# Revit family: Bordo-Basin
name_source: partatom
category: Plumbing Fixtures
units: mm (PartAtom-declared; Revit-internal decimal feet)

## family parameters
Always vertical = Yes
Cut with Voids When Loaded = No
Enable Cutting in Views = No
Maintain Annotation Orientation = No
Part Type = Normal
Room Calculation Point = No
Round Connector Dimension = Use Diameter
Shared = No
Work Plane-Based = No

## types (1)
- Lecico WHB Bordo Counter
    Color = White
    Default Elevation = 0 mm  [stored 0 ft]
    Height of WHB = 600 mm
    Manufacturer = LECICO Quality Bathroom Ceramics
    Mass = 15.00 kg
    Material = Vitreous China
    Parts Code = CTOP024
    Silver = Chrome
    Tolani Civil Projects cc URL = www.tcpbim.co.za
    URL = http://www.lecicosa.co.za

note: [stored X ft] marks values corroborated as IEEE doubles in the binary element streams (Revit-internal decimal feet)

## geometry (parser evidence)
native form markers: Sweep x3
no freeform markers — native parametric forms only
